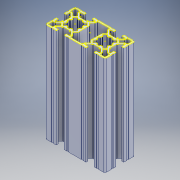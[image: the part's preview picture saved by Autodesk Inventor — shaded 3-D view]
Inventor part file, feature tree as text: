
AUTODESK INVENTOR PART (.ipt)
format: ipt  version: 2018 (Build 220112000, 112)  size: 625,664 bytes
history: native  units: mm
features: other x3, sketch x1
ambient origin geometry x8: Origin, YZ Plane, XZ Plane, XY Plane, X Axis, Y Axis, Z Axis, Center Point
bodies: Body1 (feature_tree)
feature tree (4):
  other  "Sólido1"
  sketch  "Esboço1"
  other  "Contorno projetado1"
  other  "Retangular PF30-02 - PERFIL 3060 BÁSICO(1)"
